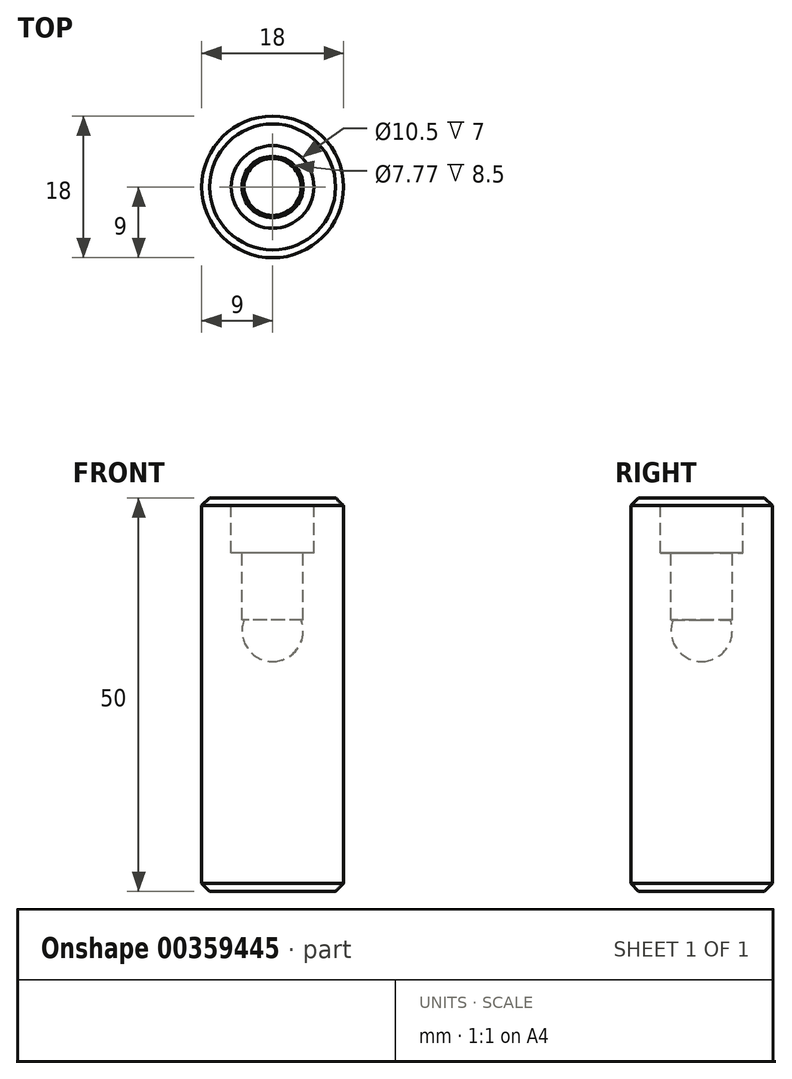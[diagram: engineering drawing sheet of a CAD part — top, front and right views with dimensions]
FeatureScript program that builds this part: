
annotation { "Feature Type Name" : "Feature", "Feature Type Description" : "" }
export const myFeature = defineFeature(function(context is Context, id is Id, definition is map)
    precondition{}
    {
        {
            assignVariable(context, id + "F0", {"name" : "BallDist", "anyValue" : 7});
        }
        {
            assignVariable(context, id + "F1", {"name" : "HandleLength", "anyValue" : 50});
        }
        {
            var Q0;
            Q0=qCreatedBy(makeId("Top.planeOp"),FACE);
            var sketch = newSketch(context, id + "F2", { "sketchPlane" : qUnion([Q0])});
            skCircle(sketch, "E0", {"center": v(0, 0) * mm, "radius": 9 * mm});
            skSolve(sketch);
        }
        {
            var Q0;
            Q0=makeQuery(id+"F2.imprint","IMPRINT",FACE,{"disambiguationData":[TD([[makeQuery(id+"F2.imprint","IMPRINT",EDGE,{"derivedFrom":sQuery(id+"F2.wireOp",EDGE,"E0")}),1.0]])]});
            extrude(context, id + "F3", {"entities" : qUnion([Q0]), "depth" : (getVariable(context, 'HandleLength')) * mm});
        }
        {
            var Q0;
            Q0=makeQuery(id+"F3.opExtrude","CAP_FACE",FACE,{"disambiguationData":[OSD([sQuery(id+"F2.wireOp",EDGE,"E0")])],"isStart":false});
            var sketch = newSketch(context, id + "F4", { "sketchPlane" : qUnion([Q0])});
            skCircle(sketch, "E1", {"center": v(0, 0) * mm, "radius": 5.25 * mm});
            skSolve(sketch);
        }
        {
            var Q0;
            Q0 = qSketchRegion(id + "F4", true);
            extrude(context, id + "F5", {"entities" : qUnion([Q0]), "operationType" : NewBodyOperationType.REMOVE, "oppositeDirection" : true, "depth" : (getVariable(context, 'BallDist')) * mm});
        }
        {
            var Q0;
            Q0=makeQuery(id+"F5.boolean.opBoolean","COPY",FACE,{"derivedFrom":makeQuery(id+"F5.opExtrude","CAP_FACE",FACE,{"disambiguationData":[OSD([sQuery(id+"F4.wireOp",EDGE,"E1")])],"isStart":false})});
            var sketch = newSketch(context, id + "F6", { "sketchPlane" : qUnion([Q0])});
            skCircle(sketch, "E2", {"center": v(0, 0) * mm, "radius": 3.88 * mm});
            skSolve(sketch);
        }
        {
            var Q0;
            Q0 = qSketchRegion(id + "F6", true);
            extrude(context, id + "F7", {"entities" : qUnion([Q0]), "operationType" : NewBodyOperationType.REMOVE, "oppositeDirection" : true, "depth" : (getVariable(context, 'BallDist') + 1.5) * mm});
        }
        {
            var Q0;
            Q0=qCreatedBy(makeId("Front.planeOp"),FACE);
            var sketch = newSketch(context, id + "F8", { "sketchPlane" : qUnion([Q0])});
            skLineSegment(sketch, "E3", {"start": v(0, 50) * mm, "end": v(0, 33.1) * mm, "construction": true});
            skPoint(sketch, "E3.endSnap0", {"position": v(0, 50) * mm});
            skLineSegment(sketch, "E4", {"start": v(0, 29.22) * mm, "end": v(0, 36.99) * mm});
            skArc(sketch, "E5", {"start": v(0, 36.99) * mm, "mid": v(-3.89, 33.1) * mm, "end": v(0, 29.22) * mm});
            skLineSegment(sketch, "E6.0", {"start": v(-5.25, 50) * mm, "end": v(5.25, 50) * mm, "construction": true});
            skSolve(sketch);
        }
        {
            var Q0;
            Q0 = qSketchRegion(id + "F8", true);
            var Q1;
            Q1=sQuery(id+"F8.wireOp",EDGE,"E4");
            revolve(context, id + "F9", {"operationType" : NewBodyOperationType.REMOVE, "entities" : qUnion([Q0]), "axis" : qUnion([Q1]), "revolveType" : RevolveType.FULL, "oppositeDirection" : true});
        }
        {
            var Q0;
            Q0=makeQuery(id+"F7.boolean.opBoolean","COPY",EDGE,{"derivedFrom":makeQuery(id+"F7.opExtrude","CAP_EDGE",EDGE,{"disambiguationData":[OSD([sQuery(id+"F6.wireOp",EDGE,"E2")])],"isStart":true})});
            var Q1;
            Q1=makeQuery(id+"F3.opExtrude","CAP_EDGE",EDGE,{"disambiguationData":[OSD([sQuery(id+"F2.wireOp",EDGE,"E0")])],"isStart":false});
            var Q2;
            Q2=makeQuery(id+"F3.opExtrude","CAP_EDGE",EDGE,{"disambiguationData":[OSD([sQuery(id+"F2.wireOp",EDGE,"E0")])],"isStart":true});
            chamfer(context, id + "F10", {"entities" : qUnion([Q0, Q1, Q2]), "width" : 1 * mm, "tangentPropagation" : true});
        }
    });
